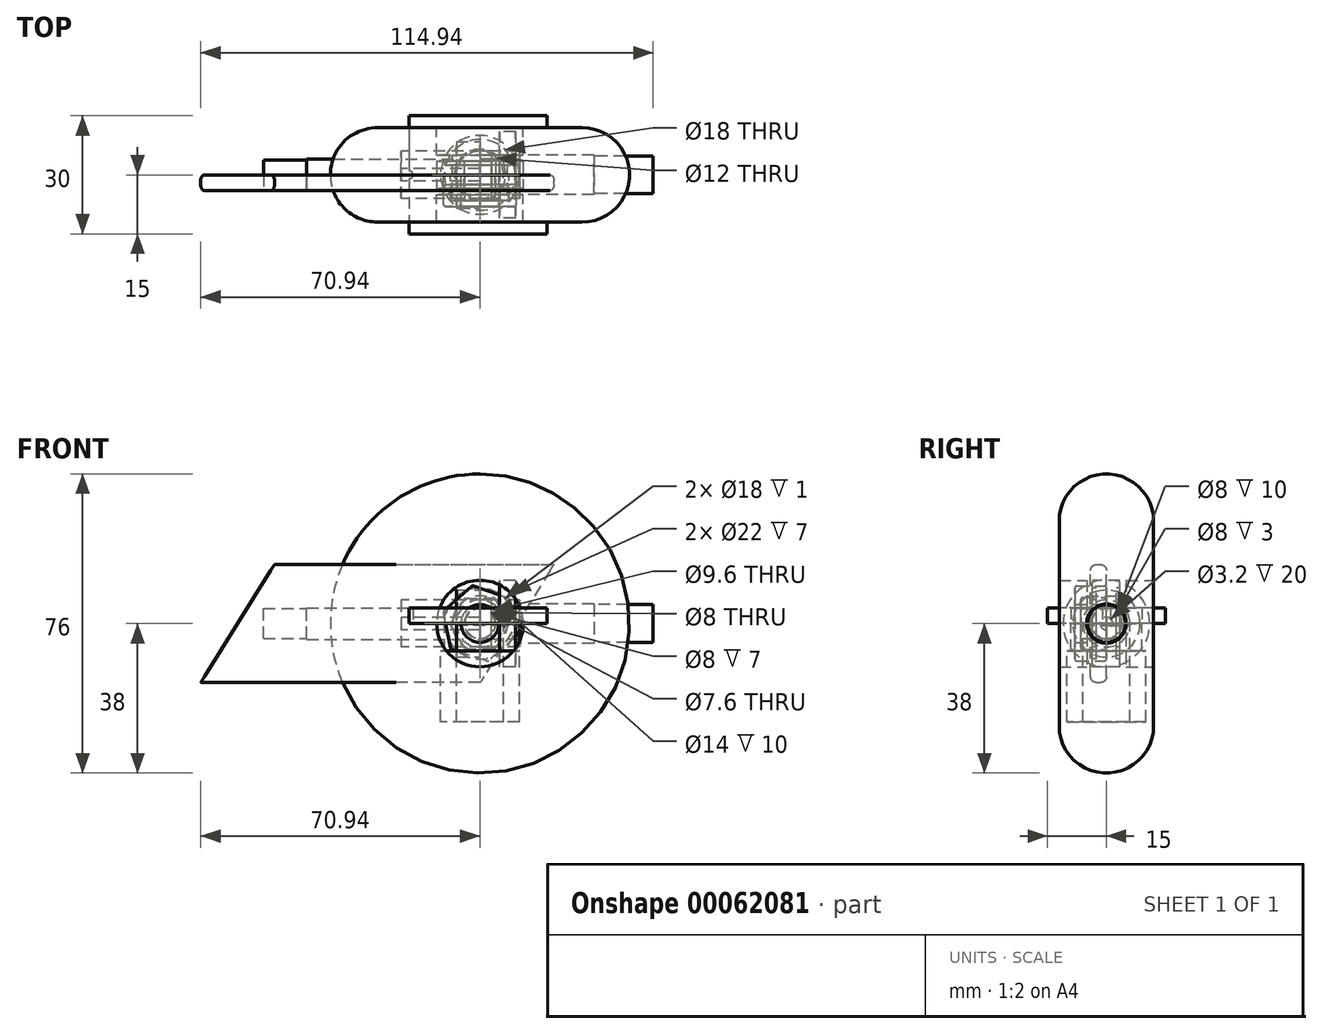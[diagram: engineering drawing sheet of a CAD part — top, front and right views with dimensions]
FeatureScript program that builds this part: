
annotation { "Feature Type Name" : "Feature", "Feature Type Description" : "" }
export const myFeature = defineFeature(function(context is Context, id is Id, definition is map)
    precondition{}
    {
        {
            assignVariable(context, id + "F0", {"name" : "h_pro", "anyValue" : 4});
        }
        {
            var Q0;
            Q0=qCreatedBy(makeId("Top.planeOp"),FACE);
            var sketch = newSketch(context, id + "F1", { "sketchPlane" : qUnion([Q0])});
            skCircle(sketch, "E0", {"center": v(0, 0) * mm, "radius": 9 * mm});
            skLineSegment(sketch, "E1.bottom", {"start": v(-18, 15) * mm, "end": v(17, 15) * mm});
            skLineSegment(sketch, "E1.top", {"start": v(-18, -15) * mm, "end": v(17, -15) * mm});
            skLineSegment(sketch, "E1.right", {"start": v(17, 15) * mm, "end": v(17, -15) * mm});
            skLineSegment(sketch, "E2", {"start": v(0, 15) * mm, "end": v(0, -15) * mm, "construction": true});
            skCircle(sketch, "E3", {"center": v(-18, 0) * mm, "radius": 1 * mm});
            skLineSegment(sketch, "E1.left", {"start": v(-18, 15) * mm, "end": v(-18, -15) * mm});
            skSolve(sketch);
        }
        {
            var Q0;
            Q0=makeQuery(id+"F1.imprint","IMPRINT",FACE,{"disambiguationData":[TD([[makeQuery(id+"F1.imprint","IMPRINT",EDGE,{"derivedFrom":sQuery(id+"F1.wireOp",EDGE,"E0")}),-1.0]])]});
            extrude(context, id + "F2", {"entities" : qUnion([Q0]), "depth" : getVariable(context, 'h_pro') * mm});
        }
        {
            var Q0;
            Q0=qCreatedBy(makeId("Front.planeOp"),FACE);
            var sketch = newSketch(context, id + "F3", { "sketchPlane" : qUnion([Q0])});
            skLineSegment(sketch, "E4", {"start": v(-70.94, -15) * mm, "end": v(-52.2, 15) * mm});
            skLineSegment(sketch, "E5", {"start": v(-52.2, 15) * mm, "end": v(18.8, 15) * mm});
            skLineSegment(sketch, "E6", {"start": v(18.8, 15) * mm, "end": v(0.06, -15) * mm});
            skLineSegment(sketch, "E7", {"start": v(0.06, -15) * mm, "end": v(-70.94, -15) * mm});
            skCircle(sketch, "E8", {"center": v(0, 0) * mm, "radius": 4 * mm});
            skLineSegment(sketch, "E9", {"start": v(-61.57, 0) * mm, "end": v(9.43, 0) * mm, "construction": true});
            skLineSegment(sketch, "E10", {"start": v(-44.28, 27.67) * mm, "end": v(0, 0) * mm, "construction": true});
            skSolve(sketch);
        }
        {
            var Q0;
            Q0=makeQuery(id+"F3.imprint","IMPRINT",FACE,{"disambiguationData":[TD([[makeQuery(id+"F3.imprint","IMPRINT",EDGE,{"derivedFrom":sQuery(id+"F3.wireOp",EDGE,"E4")}),-1.0]])]});
            extrude(context, id + "F4", {"entities" : qUnion([Q0]), "depth" : getVariable(context, 'h_pro') * mm});
        }
        {
            var Q0;
            Q0=makeQuery(id+"F4.opExtrude","CAP_EDGE",EDGE,{"disambiguationData":[OSD([sQuery(id+"F3.wireOp",EDGE,"E5")])],"isStart":false});
            var Q1;
            Q1=makeQuery(id+"F4.opExtrude","CAP_EDGE",EDGE,{"disambiguationData":[OSD([sQuery(id+"F3.wireOp",EDGE,"E5")])],"isStart":true});
            var Q2;
            Q2=makeQuery(id+"F4.opExtrude","CAP_EDGE",EDGE,{"disambiguationData":[OSD([sQuery(id+"F3.wireOp",EDGE,"E7")])],"isStart":true});
            var Q3;
            Q3=makeQuery(id+"F4.opExtrude","CAP_EDGE",EDGE,{"disambiguationData":[OSD([sQuery(id+"F3.wireOp",EDGE,"E7")])],"isStart":false});
            fillet(context, id + "F5", {"entities" : qUnion([Q0, Q1, Q2, Q3]), "radius" : 1.5 * mm, "tangentPropagation" : true, "allowEdgeOverflow" : false});
        }
        {
            var Q0;
            Q0=qCreatedBy(makeId("Front.planeOp"),FACE);
            var sketch = newSketch(context, id + "F6", { "sketchPlane" : qUnion([Q0])});
            skLineSegment(sketch, "E11", {"start": v(-10, -7) * mm, "end": v(-10, -25) * mm});
            skLineSegment(sketch, "E12", {"start": v(-10, -25) * mm, "end": v(-6, -25) * mm});
            skLineSegment(sketch, "E13", {"start": v(-6, -25) * mm, "end": v(-6, 0) * mm});
            skLineSegment(sketch, "E14", {"start": v(-6, 0) * mm, "end": v(-9, 0) * mm});
            skLineSegment(sketch, "E15", {"start": v(-9, 0) * mm, "end": v(-9, -7) * mm});
            skLineSegment(sketch, "E16", {"start": v(-9, -7) * mm, "end": v(-10, -7) * mm});
            skLineSegment(sketch, "E17", {"start": v(-6, 0) * mm, "end": v(6, 0) * mm, "construction": true});
            skLineSegment(sketch, "E18", {"start": v(0, 0) * mm, "end": v(0, -25) * mm, "construction": true});
            skLineSegment(sketch, "E19.MirrorCS", {"start": v(10, -7) * mm, "end": v(10, -25) * mm, "construction": true});
            skLineSegment(sketch, "E20.MirrorCS", {"start": v(9, -7) * mm, "end": v(10, -7) * mm, "construction": true});
            skLineSegment(sketch, "E21.MirrorCS", {"start": v(10, -25) * mm, "end": v(6, -25) * mm, "construction": true});
            skLineSegment(sketch, "E22.MirrorCS", {"start": v(6, 0) * mm, "end": v(9, 0) * mm, "construction": true});
            skLineSegment(sketch, "E23.MirrorCS", {"start": v(9, 0) * mm, "end": v(9, -7) * mm, "construction": true});
            skLineSegment(sketch, "E24.MirrorCS", {"start": v(6, -25) * mm, "end": v(6, 0) * mm, "construction": true});
            skSolve(sketch);
        }
        {
            var Q0;
            Q0=makeQuery(id+"F6.imprint","IMPRINT",FACE,{"disambiguationData":[TD([[makeQuery(id+"F6.imprint","IMPRINT",EDGE,{"derivedFrom":sQuery(id+"F6.wireOp",EDGE,"E11")}),1.0]])]});
            var Q1;
            Q1=sQuery(id+"F6.wireOp",EDGE,"E18");
            revolve(context, id + "F7", {"entities" : qUnion([Q0]), "axis" : qUnion([Q1]), "revolveType" : RevolveType.FULL});
        }
        {
            var Q0;
            Q0=makeQuery(id+"F7.opRevolve","SWEPT_EDGE",EDGE,{"disambiguationData":[OSD([sQuery(id+"F6.wireOp",EDGE,"E13"),sQuery(id+"F6.wireOp",EDGE,"E14")])]});
            chamfer(context, id + "F8", {"entities" : qUnion([Q0]), "width" : 0.5 * mm, "tangentPropagation" : true});
        }
        {
            var Q0;
            Q0=qCreatedBy(makeId("Front.planeOp"),FACE);
            var sketch = newSketch(context, id + "F9", { "sketchPlane" : qUnion([Q0])});
            skLineSegment(sketch, "E25", {"start": v(0, 0) * mm, "end": v(44, 0) * mm});
            skLineSegment(sketch, "E26", {"start": v(-20, -6) * mm, "end": v(-20, -1.6) * mm});
            skLineSegment(sketch, "E27", {"start": v(44, 0) * mm, "end": v(44, -4.8) * mm});
            skLineSegment(sketch, "E28", {"start": v(9, -5) * mm, "end": v(9, -11) * mm});
            skLineSegment(sketch, "E29", {"start": v(9, -11) * mm, "end": v(5, -11) * mm});
            skLineSegment(sketch, "E30", {"start": v(5, -11) * mm, "end": v(5, -6) * mm});
            skLineSegment(sketch, "E31", {"start": v(5, -6) * mm, "end": v(-20, -6) * mm});
            skLineSegment(sketch, "E32", {"start": v(-20, -1.6) * mm, "end": v(0, -1.6) * mm});
            skLineSegment(sketch, "E33", {"start": v(0, -1.6) * mm, "end": v(0, 0) * mm});
            skLineSegment(sketch, "E34", {"start": v(9, -5) * mm, "end": v(29, -5) * mm});
            skLineSegment(sketch, "E35", {"start": v(29, -5) * mm, "end": v(29, -4.8) * mm});
            skLineSegment(sketch, "E36", {"start": v(29, -4.8) * mm, "end": v(44, -4.8) * mm});
            skLineSegment(sketch, "E37.MirrorCS", {"start": v(29, 5) * mm, "end": v(29, 4.8) * mm, "construction": true});
            skLineSegment(sketch, "E38.MirrorCS", {"start": v(9, 5) * mm, "end": v(9, 11) * mm, "construction": true});
            skLineSegment(sketch, "E39.MirrorCS", {"start": v(-20, 6) * mm, "end": v(-20, 1.6) * mm, "construction": true});
            skLineSegment(sketch, "E40.MirrorCS", {"start": v(44, 0) * mm, "end": v(44, 4.8) * mm, "construction": true});
            skLineSegment(sketch, "E41.MirrorCS", {"start": v(9, 11) * mm, "end": v(5, 11) * mm, "construction": true});
            skLineSegment(sketch, "E42.MirrorCS", {"start": v(0, 1.6) * mm, "end": v(0, 0) * mm, "construction": true});
            skLineSegment(sketch, "E43.MirrorCS", {"start": v(29, 4.8) * mm, "end": v(44, 4.8) * mm, "construction": true});
            skLineSegment(sketch, "E44.MirrorCS", {"start": v(9, 5) * mm, "end": v(29, 5) * mm, "construction": true});
            skLineSegment(sketch, "E45.MirrorCS", {"start": v(5, 11) * mm, "end": v(5, 6) * mm, "construction": true});
            skLineSegment(sketch, "E46.MirrorCS", {"start": v(-20, 1.6) * mm, "end": v(0, 1.6) * mm, "construction": true});
            skLineSegment(sketch, "E47.MirrorCS", {"start": v(5, 6) * mm, "end": v(-20, 6) * mm, "construction": true});
            skSolve(sketch);
        }
        {
            var Q0;
            Q0=makeQuery(id+"F9.imprint","IMPRINT",FACE,{"disambiguationData":[TD([[makeQuery(id+"F9.imprint","IMPRINT",EDGE,{"derivedFrom":sQuery(id+"F9.wireOp",EDGE,"E25")}),-1.0]])]});
            var Q1;
            Q1=sQuery(id+"F9.wireOp",EDGE,"E25");
            revolve(context, id + "F10", {"entities" : qUnion([Q0]), "axis" : qUnion([Q1]), "revolveType" : RevolveType.FULL});
        }
        {
            var Q0;
            Q0=qCreatedBy(makeId("Top.planeOp"),FACE);
            var sketch = newSketch(context, id + "F11", { "sketchPlane" : qUnion([Q0])});
            skLineSegment(sketch, "E48", {"start": v(-11, 12) * mm, "end": v(-11, 5) * mm});
            skLineSegment(sketch, "E49", {"start": v(-11, 5) * mm, "end": v(-7, 5) * mm});
            skLineSegment(sketch, "E50", {"start": v(-7, 5) * mm, "end": v(-7, -5) * mm});
            skLineSegment(sketch, "E51", {"start": v(-7, -5) * mm, "end": v(-11, -5) * mm});
            skLineSegment(sketch, "E52", {"start": v(-11, -5) * mm, "end": v(-11, -12) * mm});
            skLineSegment(sketch, "E53", {"start": v(-11, -12) * mm, "end": v(-26, -12) * mm});
            skLineSegment(sketch, "E54", {"start": v(-38, 0) * mm, "end": v(-38, 0) * mm});
            skLineSegment(sketch, "E55", {"start": v(-26, 12) * mm, "end": v(-11, 12) * mm});
            skPoint(sketch, "E56.visualSharp", {"position": v(-38, 12) * mm});
            skArc(sketch, "E56.filletArc", {"start": v(-26, 12) * mm, "mid": v(-34.49, 8.49) * mm, "end": v(-38, 0) * mm});
            skPoint(sketch, "E57.visualSharp", {"position": v(-38, -12) * mm});
            skArc(sketch, "E57.filletArc", {"start": v(-38, 0) * mm, "mid": v(-34.49, -8.49) * mm, "end": v(-26, -12) * mm});
            skLineSegment(sketch, "E58", {"start": v(-7, 0) * mm, "end": v(7, 0) * mm, "construction": true});
            skLineSegment(sketch, "E59", {"start": v(0, 5) * mm, "end": v(0, -5) * mm});
            skLineSegment(sketch, "E60.MirrorCS", {"start": v(7, -5) * mm, "end": v(11, -5) * mm, "construction": true});
            skArc(sketch, "E61.MirrorCS", {"start": v(38, 0) * mm, "mid": v(34.49, -8.49) * mm, "end": v(26, -12) * mm, "construction": true});
            skArc(sketch, "E62.MirrorCS", {"start": v(26, 12) * mm, "mid": v(34.49, 8.49) * mm, "end": v(38, 0) * mm, "construction": true});
            skLineSegment(sketch, "E63.MirrorCS", {"start": v(11, -5) * mm, "end": v(11, -12) * mm, "construction": true});
            skPoint(sketch, "E64.MirrorP", {"position": v(38, 12) * mm});
            skLineSegment(sketch, "E65.MirrorCS", {"start": v(11, -12) * mm, "end": v(26, -12) * mm, "construction": true});
            skLineSegment(sketch, "E66.MirrorCS", {"start": v(38, 0) * mm, "end": v(38, 0) * mm});
            skLineSegment(sketch, "E67.MirrorCS", {"start": v(26, 12) * mm, "end": v(11, 12) * mm, "construction": true});
            skPoint(sketch, "E68.MirrorP", {"position": v(38, -12) * mm});
            skLineSegment(sketch, "E69.MirrorCS", {"start": v(7, 5) * mm, "end": v(7, -5) * mm, "construction": true});
            skLineSegment(sketch, "E70.MirrorCS", {"start": v(11, 12) * mm, "end": v(11, 5) * mm, "construction": true});
            skLineSegment(sketch, "E71.MirrorCS", {"start": v(11, 5) * mm, "end": v(7, 5) * mm, "construction": true});
            skSolve(sketch);
        }
        {
            var Q0;
            Q0=makeQuery(id+"F11.imprint","IMPRINT",FACE,{"disambiguationData":[TD([[makeQuery(id+"F11.imprint","IMPRINT",EDGE,{"derivedFrom":sQuery(id+"F11.wireOp",EDGE,"E50")}),-1.0]])]});
            var Q1;
            Q1=sQuery(id+"F11.wireOp",EDGE,"E59");
            revolve(context, id + "F12", {"entities" : qUnion([Q0]), "axis" : qUnion([Q1]), "revolveType" : RevolveType.FULL});
        }
        {
            var Q0;
            Q0=qCreatedBy(makeId("Top.planeOp"),FACE);
            var sketch = newSketch(context, id + "F13", { "sketchPlane" : qUnion([Q0])});
            skLineSegment(sketch, "E72", {"start": v(0, -4) * mm, "end": v(0, 4) * mm, "construction": true});
            skLineSegment(sketch, "E73", {"start": v(-4, 0) * mm, "end": v(4, 0) * mm, "construction": true});
            skLineSegment(sketch, "E74", {"start": v(-11, 3.5) * mm, "end": v(-9, 3.5) * mm});
            skLineSegment(sketch, "E75", {"start": v(-9, 3.5) * mm, "end": v(-9, 2.5) * mm});
            skLineSegment(sketch, "E76", {"start": v(-9, 2.5) * mm, "end": v(-6, 2.5) * mm});
            skLineSegment(sketch, "E77", {"start": v(-6, 2.5) * mm, "end": v(-6, 3.5) * mm});
            skLineSegment(sketch, "E78", {"start": v(-6, 3.5) * mm, "end": v(-4, 3.5) * mm});
            skLineSegment(sketch, "E79", {"start": v(-4, 3.5) * mm, "end": v(-4, -3.5) * mm});
            skLineSegment(sketch, "E80", {"start": v(-4, -3.5) * mm, "end": v(-6, -3.5) * mm});
            skLineSegment(sketch, "E81", {"start": v(-6, -3.5) * mm, "end": v(-6, -2.5) * mm});
            skLineSegment(sketch, "E82", {"start": v(-6, -2.5) * mm, "end": v(-9, -2.5) * mm});
            skLineSegment(sketch, "E83", {"start": v(-9, -2.5) * mm, "end": v(-9, -3.5) * mm});
            skLineSegment(sketch, "E84", {"start": v(-9, -3.5) * mm, "end": v(-11, -3.5) * mm});
            skLineSegment(sketch, "E85", {"start": v(-11, -3.5) * mm, "end": v(-11, 3.5) * mm});
            skLineSegment(sketch, "E86.MirrorCS", {"start": v(4, 3.5) * mm, "end": v(4, -3.5) * mm, "construction": true});
            skLineSegment(sketch, "E87.MirrorCS", {"start": v(6, -2.5) * mm, "end": v(9, -2.5) * mm, "construction": true});
            skLineSegment(sketch, "E88.MirrorCS", {"start": v(4, -3.5) * mm, "end": v(6, -3.5) * mm, "construction": true});
            skLineSegment(sketch, "E89.MirrorCS", {"start": v(11, 3.5) * mm, "end": v(9, 3.5) * mm, "construction": true});
            skLineSegment(sketch, "E90.MirrorCS", {"start": v(9, 3.5) * mm, "end": v(9, 2.5) * mm, "construction": true});
            skLineSegment(sketch, "E91.MirrorCS", {"start": v(6, 3.5) * mm, "end": v(4, 3.5) * mm, "construction": true});
            skLineSegment(sketch, "E92.MirrorCS", {"start": v(6, -3.5) * mm, "end": v(6, -2.5) * mm, "construction": true});
            skLineSegment(sketch, "E93.MirrorCS", {"start": v(9, -3.5) * mm, "end": v(11, -3.5) * mm, "construction": true});
            skLineSegment(sketch, "E94.MirrorCS", {"start": v(6, 2.5) * mm, "end": v(6, 3.5) * mm, "construction": true});
            skLineSegment(sketch, "E95.MirrorCS", {"start": v(9, -2.5) * mm, "end": v(9, -3.5) * mm, "construction": true});
            skLineSegment(sketch, "E96.MirrorCS", {"start": v(9, 2.5) * mm, "end": v(6, 2.5) * mm, "construction": true});
            skLineSegment(sketch, "E97.MirrorCS", {"start": v(11, -3.5) * mm, "end": v(11, 3.5) * mm, "construction": true});
            skSolve(sketch);
        }
        {
            var Q0;
            Q0=makeQuery(id+"F13.imprint","IMPRINT",FACE,{"disambiguationData":[TD([[makeQuery(id+"F13.imprint","IMPRINT",EDGE,{"derivedFrom":sQuery(id+"F13.wireOp",EDGE,"E74")}),-1.0]])]});
            var Q1;
            Q1=sQuery(id+"F13.wireOp",EDGE,"E72");
            revolve(context, id + "F14", {"entities" : qUnion([Q0]), "axis" : qUnion([Q1]), "revolveType" : RevolveType.FULL});
        }
        {
            var Q0;
            Q0=qCreatedBy(makeId("Top.planeOp"),FACE);
            var sketch = newSketch(context, id + "F15", { "sketchPlane" : qUnion([Q0])});
            skLineSegment(sketch, "E98", {"start": v(-55, 0) * mm, "end": v(-55, -3.8) * mm});
            skLineSegment(sketch, "E99", {"start": v(-6, -4) * mm, "end": v(-6, -8.5) * mm});
            skLineSegment(sketch, "E100", {"start": v(-6, -8.5) * mm, "end": v(0, -8.5) * mm});
            skLineSegment(sketch, "E101", {"start": v(0, -8.5) * mm, "end": v(0, 0) * mm});
            skLineSegment(sketch, "E102", {"start": v(0, 0) * mm, "end": v(-55, 0) * mm});
            skLineSegment(sketch, "E103", {"start": v(-55, -3.8) * mm, "end": v(-44, -3.8) * mm});
            skLineSegment(sketch, "E104", {"start": v(-44, -3.8) * mm, "end": v(-44, -4) * mm});
            skLineSegment(sketch, "E105", {"start": v(-44, -4) * mm, "end": v(-6, -4) * mm});
            skLineSegment(sketch, "E106.MirrorCS", {"start": v(-44, 3.8) * mm, "end": v(-44, 4) * mm, "construction": true});
            skLineSegment(sketch, "E107.MirrorCS", {"start": v(-55, 3.8) * mm, "end": v(-44, 3.8) * mm, "construction": true});
            skLineSegment(sketch, "E108.MirrorCS", {"start": v(0, 8.5) * mm, "end": v(0, 0) * mm, "construction": true});
            skLineSegment(sketch, "E109.MirrorCS", {"start": v(-6, 8.5) * mm, "end": v(0, 8.5) * mm, "construction": true});
            skLineSegment(sketch, "E110.MirrorCS", {"start": v(-55, 0) * mm, "end": v(-55, 3.8) * mm, "construction": true});
            skLineSegment(sketch, "E111.MirrorCS", {"start": v(-6, 4) * mm, "end": v(-6, 8.5) * mm, "construction": true});
            skLineSegment(sketch, "E112.MirrorCS", {"start": v(-44, 4) * mm, "end": v(-6, 4) * mm, "construction": true});
            skSolve(sketch);
        }
        {
            var Q0;
            Q0=makeQuery(id+"F15.imprint","IMPRINT",FACE,{"disambiguationData":[TD([[makeQuery(id+"F15.imprint","IMPRINT",EDGE,{"derivedFrom":sQuery(id+"F15.wireOp",EDGE,"E98")}),1.0]])]});
            var Q1;
            Q1=sQuery(id+"F15.wireOp",EDGE,"E102");
            revolve(context, id + "F16", {"entities" : qUnion([Q0]), "axis" : qUnion([Q1]), "revolveType" : RevolveType.FULL});
        }
        {
            var Q0;
            Q0=qCreatedBy(makeId("Right.planeOp"),FACE);
            var sketch = newSketch(context, id + "F17", { "sketchPlane" : qUnion([Q0])});
            skCircle(sketch, "E113", {"center": v(0, 0) * mm, "radius": 6 * mm});
            skCircle(sketch, "E114", {"center": v(0, 0) * mm, "radius": 4 * mm});
            skSolve(sketch);
        }
        {
            var Q0;
            Q0=makeQuery(id+"F17.imprint","IMPRINT",FACE,{"disambiguationData":[TD([[makeQuery(id+"F17.imprint","IMPRINT",EDGE,{"derivedFrom":sQuery(id+"F17.wireOp",EDGE,"E113")}),1.0]])]});
            extrude(context, id + "F18", {"entities" : qUnion([Q0]), "depth" : 10 * mm});
        }
        {
            var Q0;
            Q0 = qSketchRegion(id + "F17", true);
            extrude(context, id + "F19", {"entities" : qUnion([Q0]), "depth" : 3 * mm});
        }
        {
            var Q0;
            Q0=qCreatedBy(makeId("Front.planeOp"),FACE);
            var sketch = newSketch(context, id + "F20", { "sketchPlane" : qUnion([Q0])});
            skCircle(sketch, "E115.cCircle", {"center": v(0, 0) * mm, "radius": 6.5 * mm, "construction": true});
            skLineSegment(sketch, "E115.0", {"start": v(7.5, 0.21) * mm, "end": v(3.94, -6.4) * mm});
            skLineSegment(sketch, "E115.1", {"start": v(3.94, -6.4) * mm, "end": v(-3.57, -6.6) * mm});
            skLineSegment(sketch, "E115.2", {"start": v(-3.57, -6.6) * mm, "end": v(-7.5, -0.21) * mm});
            skLineSegment(sketch, "E115.3", {"start": v(-7.5, -0.21) * mm, "end": v(-3.94, 6.4) * mm});
            skLineSegment(sketch, "E115.4", {"start": v(-3.94, 6.4) * mm, "end": v(3.57, 6.6) * mm});
            skLineSegment(sketch, "E115.5", {"start": v(3.57, 6.6) * mm, "end": v(7.5, 0.21) * mm});
            skPoint(sketch, "E115.0.midPoint", {"position": v(5.72, -3.09) * mm});
            skCircle(sketch, "E116", {"center": v(0, 0) * mm, "radius": 3.8 * mm});
            skSolve(sketch);
        }
        {
            var Q0;
            Q0=makeQuery(id+"F20.imprint","IMPRINT",FACE,{"disambiguationData":[TD([[makeQuery(id+"F20.imprint","IMPRINT",EDGE,{"derivedFrom":sQuery(id+"F20.wireOp",EDGE,"E115.0")}),-1.0]])]});
            extrude(context, id + "F21", {"entities" : qUnion([Q0]), "depth" : 6.5 * mm});
        }
        {
            var Q0;
            Q0=makeQuery(id+"F21.opExtrude","CAP_EDGE",EDGE,{"disambiguationData":[OSD([sQuery(id+"F20.wireOp",EDGE,"E115.4")])],"isStart":true});
            var Q1;
            Q1=makeQuery(id+"F21.opExtrude","CAP_EDGE",EDGE,{"disambiguationData":[OSD([sQuery(id+"F20.wireOp",EDGE,"E115.3")])],"isStart":true});
            var Q2;
            Q2=makeQuery(id+"F21.opExtrude","CAP_EDGE",EDGE,{"disambiguationData":[OSD([sQuery(id+"F20.wireOp",EDGE,"E115.2")])],"isStart":true});
            var Q3;
            Q3=makeQuery(id+"F21.opExtrude","CAP_EDGE",EDGE,{"disambiguationData":[OSD([sQuery(id+"F20.wireOp",EDGE,"E115.1")])],"isStart":true});
            var Q4;
            Q4=makeQuery(id+"F21.opExtrude","CAP_EDGE",EDGE,{"disambiguationData":[OSD([sQuery(id+"F20.wireOp",EDGE,"E115.0")])],"isStart":true});
            var Q5;
            Q5=makeQuery(id+"F21.opExtrude","CAP_EDGE",EDGE,{"disambiguationData":[OSD([sQuery(id+"F20.wireOp",EDGE,"E115.5")])],"isStart":true});
            var Q6;
            Q6=makeQuery(id+"F21.opExtrude","CAP_EDGE",EDGE,{"disambiguationData":[OSD([sQuery(id+"F20.wireOp",EDGE,"E115.1")])],"isStart":false});
            var Q7;
            Q7=makeQuery(id+"F21.opExtrude","CAP_EDGE",EDGE,{"disambiguationData":[OSD([sQuery(id+"F20.wireOp",EDGE,"E115.2")])],"isStart":false});
            var Q8;
            Q8=makeQuery(id+"F21.opExtrude","CAP_EDGE",EDGE,{"disambiguationData":[OSD([sQuery(id+"F20.wireOp",EDGE,"E115.0")])],"isStart":false});
            var Q9;
            Q9=makeQuery(id+"F21.opExtrude","CAP_EDGE",EDGE,{"disambiguationData":[OSD([sQuery(id+"F20.wireOp",EDGE,"E115.5")])],"isStart":false});
            var Q10;
            Q10=makeQuery(id+"F21.opExtrude","CAP_EDGE",EDGE,{"disambiguationData":[OSD([sQuery(id+"F20.wireOp",EDGE,"E115.4")])],"isStart":false});
            var Q11;
            Q11=makeQuery(id+"F21.opExtrude","CAP_EDGE",EDGE,{"disambiguationData":[OSD([sQuery(id+"F20.wireOp",EDGE,"E115.3")])],"isStart":false});
            var Q12;
            Q12=makeQuery(id+"F21.opExtrude","SWEPT_EDGE",EDGE,{"disambiguationData":[OSD([sQuery(id+"F20.wireOp",EDGE,"E115.3"),sQuery(id+"F20.wireOp",EDGE,"E115.4")])]});
            var Q13;
            Q13=makeQuery(id+"F21.opExtrude","SWEPT_EDGE",EDGE,{"disambiguationData":[OSD([sQuery(id+"F20.wireOp",EDGE,"E115.4"),sQuery(id+"F20.wireOp",EDGE,"E115.5")])]});
            var Q14;
            Q14=makeQuery(id+"F21.opExtrude","SWEPT_EDGE",EDGE,{"disambiguationData":[OSD([sQuery(id+"F20.wireOp",EDGE,"E115.0"),sQuery(id+"F20.wireOp",EDGE,"E115.5")])]});
            var Q15;
            Q15=makeQuery(id+"F21.opExtrude","SWEPT_EDGE",EDGE,{"disambiguationData":[OSD([sQuery(id+"F20.wireOp",EDGE,"E115.2"),sQuery(id+"F20.wireOp",EDGE,"E115.3")])]});
            var Q16;
            Q16=makeQuery(id+"F21.opExtrude","SWEPT_EDGE",EDGE,{"disambiguationData":[OSD([sQuery(id+"F20.wireOp",EDGE,"E115.1"),sQuery(id+"F20.wireOp",EDGE,"E115.2")])]});
            var Q17;
            Q17=makeQuery(id+"F21.opExtrude","SWEPT_EDGE",EDGE,{"disambiguationData":[OSD([sQuery(id+"F20.wireOp",EDGE,"E115.0"),sQuery(id+"F20.wireOp",EDGE,"E115.1")])]});
            fillet(context, id + "F22", {"entities" : qUnion([Q0, Q1, Q2, Q3, Q4, Q5, Q6, Q7, Q8, Q9, Q10, Q11, Q12, Q13, Q14, Q15, Q16, Q17]), "radius" : 0.5 * mm, "tangentPropagation" : true, "allowEdgeOverflow" : false});
        }
        {
            var Q0;
            Q0=qCreatedBy(makeId("Front.planeOp"),FACE);
            var sketch = newSketch(context, id + "F23", { "sketchPlane" : qUnion([Q0])});
            skPoint(sketch, "E117.0.midPoint", {"position": v(5.63, -6.37) * mm});
            skCircle(sketch, "E117.cCircle", {"center": v(0, 0) * mm, "radius": 8.5 * mm, "construction": true});
            skLineSegment(sketch, "E117.0", {"start": v(9.3, -3.12) * mm, "end": v(1.95, -9.62) * mm});
            skLineSegment(sketch, "E117.1", {"start": v(1.95, -9.62) * mm, "end": v(-7.36, -6.5) * mm});
            skLineSegment(sketch, "E117.2", {"start": v(-7.36, -6.5) * mm, "end": v(-9.3, 3.12) * mm});
            skLineSegment(sketch, "E117.3", {"start": v(-9.3, 3.12) * mm, "end": v(-1.95, 9.62) * mm});
            skLineSegment(sketch, "E117.4", {"start": v(-1.95, 9.62) * mm, "end": v(7.36, 6.5) * mm});
            skLineSegment(sketch, "E117.5", {"start": v(7.36, 6.5) * mm, "end": v(9.3, -3.12) * mm});
            skCircle(sketch, "E118", {"center": v(0, 0) * mm, "radius": 4.8 * mm});
            skSolve(sketch);
        }
        {
            var Q0;
            Q0=makeQuery(id+"F23.imprint","IMPRINT",FACE,{"disambiguationData":[TD([[makeQuery(id+"F23.imprint","IMPRINT",EDGE,{"derivedFrom":sQuery(id+"F23.wireOp",EDGE,"E117.0")}),-1.0]])]});
            extrude(context, id + "F24", {"entities" : qUnion([Q0]), "depth" : 8 * mm});
        }
        {
            var Q0;
            Q0=makeQuery(id+"F24.opExtrude","SWEPT_FACE",FACE,{"disambiguationData":[OSD([sQuery(id+"F23.wireOp",EDGE,"E117.1")])]});
            var Q1;
            Q1=makeQuery(id+"F24.opExtrude","SWEPT_FACE",FACE,{"disambiguationData":[OSD([sQuery(id+"F23.wireOp",EDGE,"E117.2")])]});
            var Q2;
            Q2=makeQuery(id+"F24.opExtrude","SWEPT_FACE",FACE,{"disambiguationData":[OSD([sQuery(id+"F23.wireOp",EDGE,"E117.3")])]});
            var Q3;
            Q3=makeQuery(id+"F24.opExtrude","SWEPT_FACE",FACE,{"disambiguationData":[OSD([sQuery(id+"F23.wireOp",EDGE,"E117.4")])]});
            var Q4;
            Q4=makeQuery(id+"F24.opExtrude","SWEPT_FACE",FACE,{"disambiguationData":[OSD([sQuery(id+"F23.wireOp",EDGE,"E117.5")])]});
            var Q5;
            Q5=makeQuery(id+"F24.opExtrude","SWEPT_FACE",FACE,{"disambiguationData":[OSD([sQuery(id+"F23.wireOp",EDGE,"E117.0")])]});
            fillet(context, id + "F25", {"entities" : qUnion([Q0, Q1, Q2, Q3, Q4, Q5]), "radius" : 0.5 * mm, "tangentPropagation" : true, "allowEdgeOverflow" : false});
        }
    });
